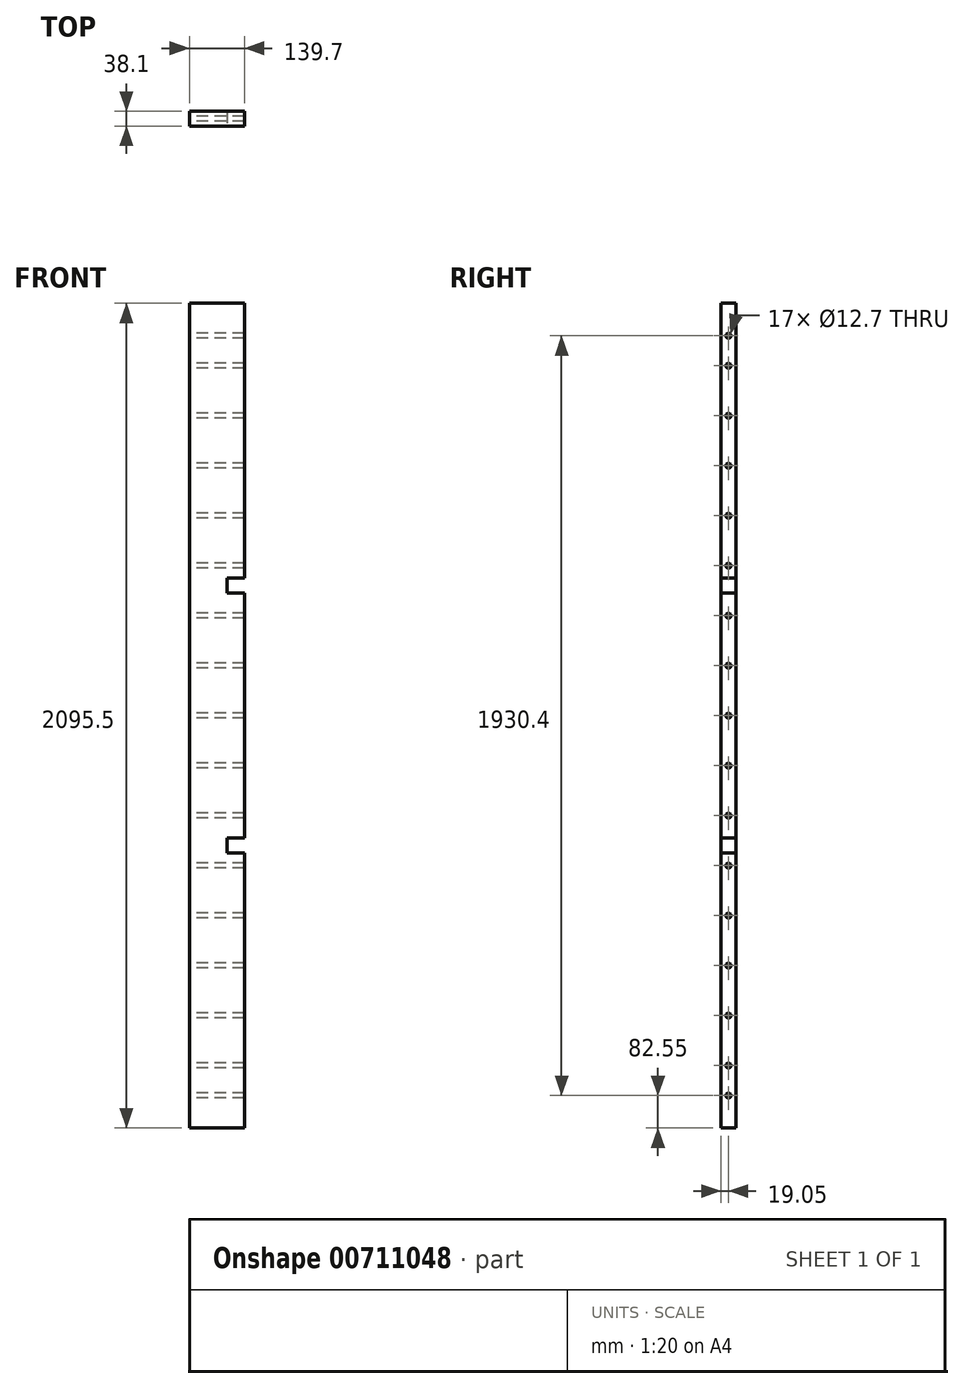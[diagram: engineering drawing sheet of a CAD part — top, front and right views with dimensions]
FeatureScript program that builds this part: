
annotation { "Feature Type Name" : "Feature", "Feature Type Description" : "" }
export const myFeature = defineFeature(function(context is Context, id is Id, definition is map)
    precondition{}
    {
        {
            var Q0;
            Q0=qCreatedBy(makeId("Top.planeOp"),FACE);
            var sketch = newSketch(context, id + "F0", { "sketchPlane" : qUnion([Q0])});
            skLineSegment(sketch, "E0.bottom", {"start": v(69.85, 19.05) * mm, "end": v(-69.85, 19.05) * mm});
            skLineSegment(sketch, "E0.top", {"start": v(69.85, -19.05) * mm, "end": v(-69.85, -19.05) * mm});
            skLineSegment(sketch, "E0.left", {"start": v(69.85, 19.05) * mm, "end": v(69.85, -19.05) * mm});
            skLineSegment(sketch, "E0.right", {"start": v(-69.85, 19.05) * mm, "end": v(-69.85, -19.05) * mm});
            skPoint(sketch, "E0.middle", {"position": v(0, 0) * mm});
            skSolve(sketch);
        }
        {
            var Q0;
            Q0=makeQuery(id+"F0.imprint","IMPRINT",FACE,{"disambiguationData":[TD([[makeQuery(id+"F0.imprint","IMPRINT",EDGE,{"derivedFrom":sQuery(id+"F0.wireOp",EDGE,"E0.bottom")}),1.0]])]});
            extrude(context, id + "F1", {"entities" : qUnion([Q0]), "depth" : 2095.5 * mm, "offsetDistance" : 25.4 * mm});
        }
        {
            var Q0;
            Q0=makeQuery(id+"F1.opExtrude","SWEPT_FACE",FACE,{"disambiguationData":[OSD([sQuery(id+"F0.wireOp",EDGE,"E0.right")])]});
            var sketch = newSketch(context, id + "F2", { "sketchPlane" : qUnion([Q0])});
            skLineSegment(sketch, "E1", {"start": v(-19.05, 1047.75) * mm, "end": v(19.05, 1047.75) * mm});
            skCircle(sketch, "E2", {"center": v(0, 1047.75) * mm, "radius": 6.35 * mm});
            skCircle(sketch, "E3.0.1.0", {"center": v(0, 1174.75) * mm, "radius": 6.35 * mm});
            skCircle(sketch, "E3.0.2.0", {"center": v(0, 1301.75) * mm, "radius": 6.35 * mm});
            skCircle(sketch, "E3.0.3.0", {"center": v(0, 1428.75) * mm, "radius": 6.35 * mm});
            skCircle(sketch, "E3.0.4.0", {"center": v(0, 1555.75) * mm, "radius": 6.35 * mm});
            skCircle(sketch, "E3.0.5.0", {"center": v(0, 1682.75) * mm, "radius": 6.35 * mm});
            skCircle(sketch, "E3.0.6.0", {"center": v(0, 1809.75) * mm, "radius": 6.35 * mm});
            skCircle(sketch, "E3.0.7.0", {"center": v(0, 1936.75) * mm, "radius": 6.35 * mm});
            skLineSegment(sketch, "E3.direction1", {"start": v(0, 1047.75) * mm, "end": v(25.4, 1047.75) * mm, "construction": true});
            skLineSegment(sketch, "E3.direction2", {"start": v(0, 1047.75) * mm, "end": v(0, 1174.75) * mm, "construction": true});
            skCircle(sketch, "E4.MirrorC", {"center": v(0, 920.75) * mm, "radius": 6.35 * mm});
            skCircle(sketch, "E5.MirrorC", {"center": v(0, 666.75) * mm, "radius": 6.35 * mm});
            skCircle(sketch, "E6.MirrorC", {"center": v(0, 539.75) * mm, "radius": 6.35 * mm});
            skCircle(sketch, "E7.MirrorC", {"center": v(0, 412.75) * mm, "radius": 6.35 * mm});
            skCircle(sketch, "E8.MirrorC", {"center": v(0, 285.75) * mm, "radius": 6.35 * mm});
            skCircle(sketch, "E9.MirrorC", {"center": v(0, 158.75) * mm, "radius": 6.35 * mm});
            skCircle(sketch, "E10.MirrorC", {"center": v(0, 793.75) * mm, "radius": 6.35 * mm});
            skCircle(sketch, "E11", {"center": v(0, 2012.95) * mm, "radius": 6.35 * mm});
            skCircle(sketch, "E12.MirrorC", {"center": v(0, 82.55) * mm, "radius": 6.35 * mm});
            skSolve(sketch);
        }
        {
            var Q0;
            Q0 = qSketchRegion(id + "F2", true);
            extrude(context, id + "F3", {"entities" : qUnion([Q0]), "operationType" : NewBodyOperationType.REMOVE, "oppositeDirection" : true, "depth" : 152.4 * mm, "offsetDistance" : 25.4 * mm});
        }
        {
            var Q0;
            Q0=makeQuery(id+"F1.opExtrude","SWEPT_FACE",FACE,{"disambiguationData":[OSD([sQuery(id+"F0.wireOp",EDGE,"E0.left")])]});
            var sketch = newSketch(context, id + "F4", { "sketchPlane" : qUnion([Q0])});
            skLineSegment(sketch, "E13.0", {"start": v(19.05, 1397) * mm, "end": v(-19.05, 1397) * mm});
            skLineSegment(sketch, "E14.0", {"start": v(19.05, 698.5) * mm, "end": v(-19.05, 698.5) * mm});
            skLineSegment(sketch, "E15.0", {"start": v(19.05, 1358.9) * mm, "end": v(-19.05, 1358.9) * mm});
            skLineSegment(sketch, "E16.0", {"start": v(19.05, 736.6) * mm, "end": v(-19.05, 736.6) * mm});
            skLineSegment(sketch, "E17", {"start": v(-19.05, 1047.75) * mm, "end": v(19.05, 1047.75) * mm});
            skSolve(sketch);
        }
        {
            var Q0;
            Q0 = qSketchRegion(id + "F4", true);
            var Q1;
            {var subQ0=sQuery(id+"F4.wireOp",EDGE,"E14.0");Q1=makeQuery(id+"F4.imprint","IMPRINT",FACE,{"disambiguationData":[TD([[makeQuery(id+"F4.imprint","IMPRINT",EDGE,{"derivedFrom":subQ0}),-1.0]])]});}
            var Q2;
            {var subQ0=sQuery(id+"F4.wireOp",EDGE,"E13.0");Q2=makeQuery(id+"F4.imprint","IMPRINT",FACE,{"disambiguationData":[TD([[makeQuery(id+"F4.imprint","IMPRINT",EDGE,{"derivedFrom":subQ0}),1.0]])]});}
            extrude(context, id + "F5", {"entities" : qUnion([Q0, Q1, Q2]), "operationType" : NewBodyOperationType.REMOVE, "oppositeDirection" : true, "depth" : 44.45 * mm, "offsetDistance" : 25.4 * mm});
        }
    });
